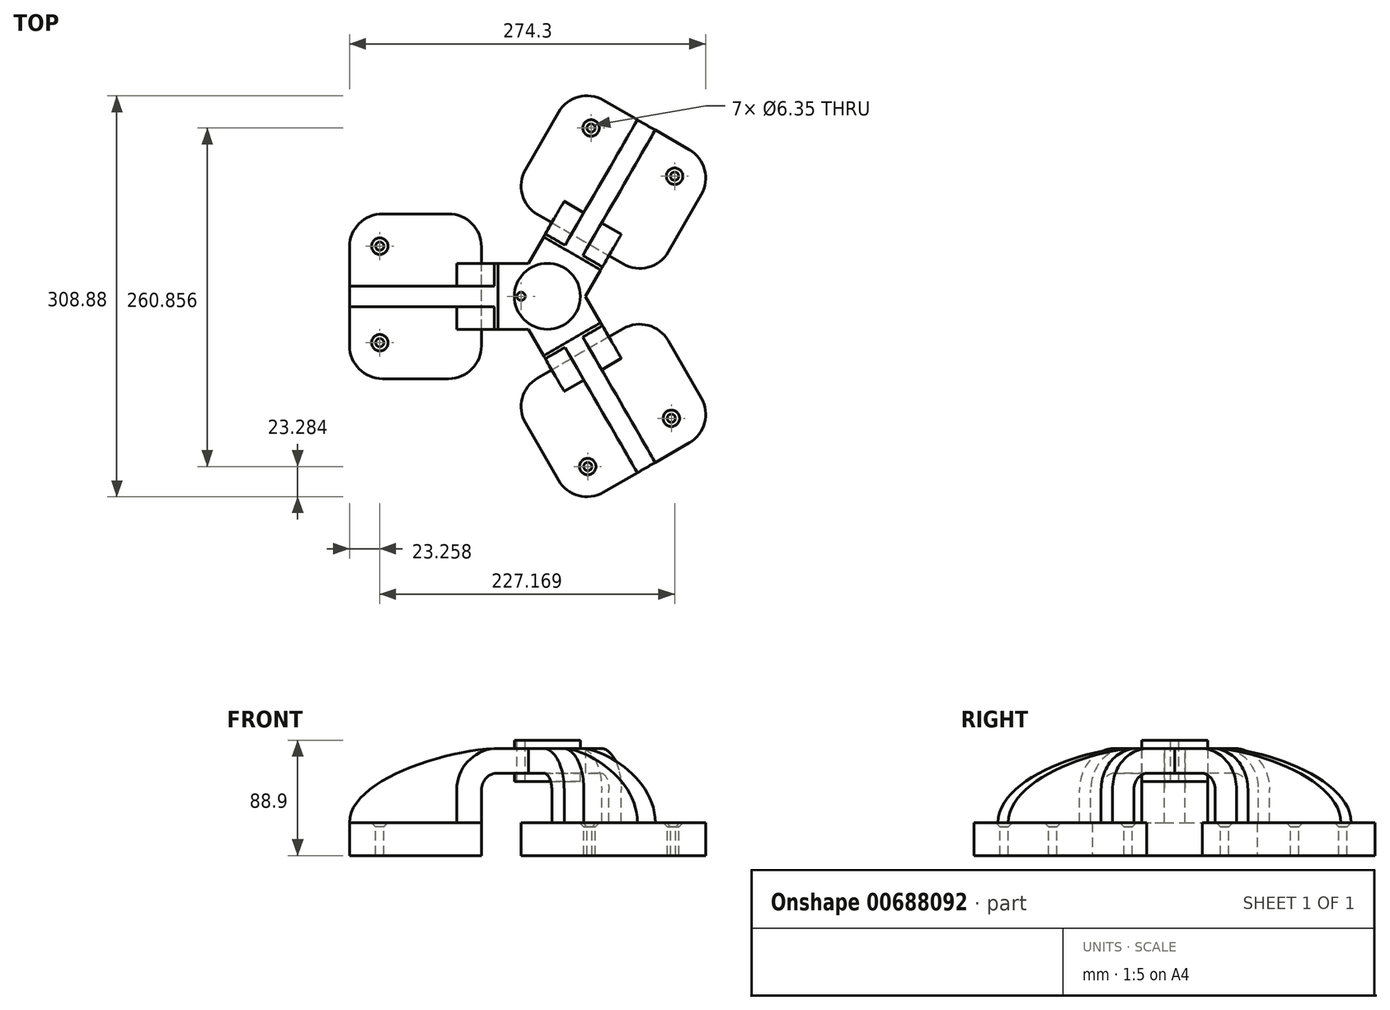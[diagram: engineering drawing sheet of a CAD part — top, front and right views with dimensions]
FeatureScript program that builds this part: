
annotation { "Feature Type Name" : "Feature", "Feature Type Description" : "" }
export const myFeature = defineFeature(function(context is Context, id is Id, definition is map)
    precondition{}
    {
        {
            var Q0;
            Q0=qCreatedBy(makeId("Front.planeOp"),FACE);
            var sketch = newSketch(context, id + "F0", { "sketchPlane" : qUnion([Q0])});
            skLineSegment(sketch, "E0.bottom", {"start": v(50.8, 12.7) * mm, "end": v(-50.8, 12.7) * mm});
            skLineSegment(sketch, "E0.top", {"start": v(50.8, -12.7) * mm, "end": v(-50.8, -12.7) * mm});
            skLineSegment(sketch, "E0.left", {"start": v(50.8, 12.7) * mm, "end": v(50.8, -12.7) * mm});
            skLineSegment(sketch, "E0.right", {"start": v(-50.8, 12.7) * mm, "end": v(-50.8, -12.7) * mm});
            skPoint(sketch, "E0.middle", {"position": v(0, 0) * mm});
            skLineSegment(sketch, "E1.bottom", {"start": v(76.2, 76.2) * mm, "end": v(127, 76.2) * mm});
            skLineSegment(sketch, "E1.top", {"start": v(76.2, 44.45) * mm, "end": v(127, 44.45) * mm});
            skLineSegment(sketch, "E1.left", {"start": v(76.2, 76.2) * mm, "end": v(76.2, 44.45) * mm});
            skLineSegment(sketch, "E1.right", {"start": v(127, 76.2) * mm, "end": v(127, 44.45) * mm});
            skLineSegment(sketch, "E2", {"start": v(50.8, 12.7) * mm, "end": v(50.8, 38.1) * mm});
            skArc(sketch, "E3", {"start": v(50.8, 38.1) * mm, "mid": v(54.52, 47.08) * mm, "end": v(63.5, 50.8) * mm});
            skLineSegment(sketch, "E4", {"start": v(63.5, 50.8) * mm, "end": v(101.6, 50.8) * mm});
            skLineSegment(sketch, "E5.0", {"start": v(63.5, 69.85) * mm, "end": v(101.6, 69.85) * mm});
            skArc(sketch, "E5.1", {"start": v(31.75, 38.1) * mm, "mid": v(41.05, 60.55) * mm, "end": v(63.5, 69.85) * mm});
            skLineSegment(sketch, "E5.2", {"start": v(31.75, 12.7) * mm, "end": v(31.75, 38.1) * mm});
            skFitSpline(sketch, "E6", {"points": [v(-50.8, 12.7) * mm, v(63.5, 69.85) * mm], "startDerivative": vector(-1.6, 93) * mm, "endDerivative": vector(136.62, 4.63) * mm});
            skLineSegment(sketch, "E7", {"start": v(101.6, 76.2) * mm, "end": v(101.6, 44.45) * mm});
            skSolve(sketch);
        }
        {
            var Q0;
            Q0=makeQuery(id+"F0.imprint","IMPRINT",FACE,{"disambiguationData":[TD([[makeQuery(id+"F0.imprint","IMPRINT",EDGE,{"derivedFrom":sQuery(id+"F0.wireOp",EDGE,"E0.top")}),-1.0]])]});
            extrude(context, id + "F1", {"entities" : qUnion([Q0]), "endBound" : BoundingType.SYMMETRIC, "depth" : 127 * mm, "offsetDistance" : 25.4 * mm});
        }
        {
            var Q0;
            {var subQ1=sQuery(id+"F0.wireOp",EDGE,"E2");Q0=makeQuery(id+"F0.imprint","IMPRINT",FACE,{"disambiguationData":[TD([[makeQuery(id+"F0.imprint","IMPRINT",EDGE,{"derivedFrom":subQ1}),1.0]])]});}
            var Q1;
            {var subQ0=sQuery(id+"F0.wireOp",EDGE,"E5.0");var subQ1=sQuery(id+"F0.wireOp",EDGE,"E1.left");var subQ2=makeQuery(id+"F0.imprint","INTERSECT",VERTEX,{"derivedFrom":[subQ1,subQ0]});Q1=makeQuery(id+"F0.imprint","IMPRINT",FACE,{"disambiguationData":[TD([[makeQuery(id+"F0.imprint","IMPRINT",EDGE,{"disambiguationData":[TD([[subQ2,-1.0]])],"derivedFrom":subQ1}),1.0]])]});}
            extrude(context, id + "F2", {"entities" : qUnion([Q0, Q1]), "operationType" : NewBodyOperationType.ADD, "endBound" : BoundingType.SYMMETRIC, "depth" : 50.8 * mm, "offsetDistance" : 25.4 * mm});
        }
        {
            var Q0;
            {var subQ3=sQuery(id+"F0.wireOp",EDGE,"E5.2");Q0=makeQuery(id+"F0.imprint","IMPRINT",FACE,{"disambiguationData":[TD([[makeQuery(id+"F0.imprint","IMPRINT",EDGE,{"derivedFrom":subQ3}),1.0]])]});}
            extrude(context, id + "F3", {"entities" : qUnion([Q0]), "operationType" : NewBodyOperationType.ADD, "endBound" : BoundingType.SYMMETRIC, "depth" : 15.88 * mm, "offsetDistance" : 25.4 * mm});
        }
        {
            var Q0;
            {var subQ4=sQuery(id+"F0.wireOp",EDGE,"E1.right");Q0=makeQuery(id+"F0.imprint","IMPRINT",FACE,{"disambiguationData":[TD([[makeQuery(id+"F0.imprint","IMPRINT",EDGE,{"derivedFrom":subQ4}),-1.0]])]});}
            var Q1;
            Q1=sQuery(id+"F0.wireOp",EDGE,"E7");
            revolve(context, id + "F4", {"operationType" : NewBodyOperationType.ADD, "entities" : qUnion([Q0]), "axis" : qUnion([Q1]), "revolveType" : RevolveType.FULL});
        }
        {
            var Q0;
            {var subQ4=sQuery(id+"F0.wireOp",EDGE,"E0.bottom");var subQ5=sQuery(id+"F0.wireOp",EDGE,"E0.right");var subQ6=sQuery(id+"F0.wireOp",EDGE,"E0.left");Q0=makeQuery(id+"F3.boolean.opBoolean","SPLIT",FACE,{"disambiguationData":[TD([makeQuery(id+"F1.opExtrude","CAP_FACE",FACE,{"disambiguationData":[OSD([subQ4,sQuery(id+"F0.wireOp",EDGE,"E0.top"),subQ6,subQ5])],"isStart":false})])],"derivedFrom":makeQuery(id+"F1.opExtrude","SWEPT_FACE",FACE,{"disambiguationData":[OSD([subQ4])]})});}
            var sketch = newSketch(context, id + "F5", { "sketchPlane" : qUnion([Q0])});
            skPoint(sketch, "E8", {"position": v(-27.54, -35.72) * mm});
            skPoint(sketch, "E8.positionSnap0", {"position": v(-50.8, -35.72) * mm});
            skPoint(sketch, "E9", {"position": v(-27.54, 38.63) * mm});
            skSolve(sketch);
        }
        {
            var Q0;
            Q0=sQuery(id+"F5.wireOp",VERTEX,"E8");
            var Q1;
            Q1=sQuery(id+"F5.wireOp",VERTEX,"E9");
            var Q2;
            Q2=makeQuery(id+"F1.opExtrude","SWEPT_BODY",BODY,{"disambiguationData":[OSD([sQuery(id+"F0.wireOp",EDGE,"E0.bottom"),sQuery(id+"F0.wireOp",EDGE,"E0.top"),sQuery(id+"F0.wireOp",EDGE,"E0.left"),sQuery(id+"F0.wireOp",EDGE,"E0.right")])]});
            hole(context, id + "F6", {"style" : HoleStyle.C_SINK, "endStyle" : HoleEndStyle.THROUGH, "holeDiameter" : 6.35 * mm, "cSinkDiameter" : 12.7 * mm, "cSinkAngle" : 90 * degree, "majorDiameter" : 6.35 * mm, "isTappedThrough" : true, "tappedDepth" : 12.7 * mm, "tapClearance" : 3, "locations" : qUnion([Q0, Q1]), "scope" : qUnion([Q2])});
        }
        {
            var Q0;
            Q0=makeQuery(id+"F1.opExtrude","SWEPT_BODY",BODY,{"disambiguationData":[OSD([sQuery(id+"F0.wireOp",EDGE,"E0.bottom"),sQuery(id+"F0.wireOp",EDGE,"E0.top"),sQuery(id+"F0.wireOp",EDGE,"E0.left"),sQuery(id+"F0.wireOp",EDGE,"E0.right")])]});
            var Q1;
            Q1=sQuery(id+"F0.wireOp",EDGE,"E7");
            circularPattern(context, id + "F7", {"operationType" : NewBodyOperationType.ADD, "entities" : qUnion([Q0]), "axis" : qUnion([Q1]), "angle" : 360 * degree, "instanceCount" : 3, "equalSpace" : true});
        }
        {
            var Q0;
            Q0=makeQuery(id+"F4.opRevolve","SWEPT_FACE",FACE,{"disambiguationData":[OSD([sQuery(id+"F0.wireOp",EDGE,"E1.bottom")])]});
            var sketch = newSketch(context, id + "F8", { "sketchPlane" : qUnion([Q0])});
            skPoint(sketch, "E10", {"position": v(81.33, 0) * mm});
            skSolve(sketch);
        }
        {
            var Q0;
            Q0=sQuery(id+"F8.wireOp",VERTEX,"E10");
            var Q1;
            Q1=makeQuery(id+"F1.opExtrude","SWEPT_BODY",BODY,{"disambiguationData":[OSD([sQuery(id+"F0.wireOp",EDGE,"E0.bottom"),sQuery(id+"F0.wireOp",EDGE,"E0.top"),sQuery(id+"F0.wireOp",EDGE,"E0.left"),sQuery(id+"F0.wireOp",EDGE,"E0.right")])]});
            hole(context, id + "F9", {"style" : HoleStyle.SIMPLE, "endStyle" : HoleEndStyle.THROUGH, "holeDiameter" : 6.35 * mm, "majorDiameter" : 6.35 * mm, "isTappedThrough" : true, "tappedDepth" : 12.7 * mm, "tapClearance" : 3, "locations" : qUnion([Q0]), "scope" : qUnion([Q1])});
        }
        {
            var Q0;
            Q0=makeQuery(id+"F1.opExtrude","CAP_EDGE",EDGE,{"disambiguationData":[OSD([sQuery(id+"F0.wireOp",EDGE,"E0.right")])],"isStart":false});
            var Q1;
            Q1=makeQuery(id+"F7.opPattern","COPY",EDGE,{"derivedFrom":makeQuery(id+"F1.opExtrude","CAP_EDGE",EDGE,{"disambiguationData":[OSD([sQuery(id+"F0.wireOp",EDGE,"E0.right")])],"isStart":true}),"instanceName":"2"});
            var Q2;
            Q2=makeQuery(id+"F7.opPattern","COPY",EDGE,{"derivedFrom":makeQuery(id+"F1.opExtrude","CAP_EDGE",EDGE,{"disambiguationData":[OSD([sQuery(id+"F0.wireOp",EDGE,"E0.right")])],"isStart":false}),"instanceName":"2"});
            var Q3;
            Q3=makeQuery(id+"F7.opPattern","COPY",EDGE,{"derivedFrom":makeQuery(id+"F1.opExtrude","CAP_EDGE",EDGE,{"disambiguationData":[OSD([sQuery(id+"F0.wireOp",EDGE,"E0.right")])],"isStart":true}),"instanceName":"1"});
            var Q4;
            Q4=makeQuery(id+"F7.opPattern","COPY",EDGE,{"derivedFrom":makeQuery(id+"F1.opExtrude","CAP_EDGE",EDGE,{"disambiguationData":[OSD([sQuery(id+"F0.wireOp",EDGE,"E0.left")])],"isStart":true}),"instanceName":"1"});
            var Q5;
            Q5=makeQuery(id+"F7.opPattern","COPY",EDGE,{"derivedFrom":makeQuery(id+"F1.opExtrude","CAP_EDGE",EDGE,{"disambiguationData":[OSD([sQuery(id+"F0.wireOp",EDGE,"E0.left")])],"isStart":false}),"instanceName":"2"});
            var Q6;
            Q6=makeQuery(id+"F1.opExtrude","CAP_EDGE",EDGE,{"disambiguationData":[OSD([sQuery(id+"F0.wireOp",EDGE,"E0.left")])],"isStart":false});
            var Q7;
            Q7=makeQuery(id+"F7.opPattern","COPY",EDGE,{"derivedFrom":makeQuery(id+"F1.opExtrude","CAP_EDGE",EDGE,{"disambiguationData":[OSD([sQuery(id+"F0.wireOp",EDGE,"E0.right")])],"isStart":false}),"instanceName":"1"});
            var Q8;
            Q8=makeQuery(id+"F7.opPattern","COPY",EDGE,{"derivedFrom":makeQuery(id+"F1.opExtrude","CAP_EDGE",EDGE,{"disambiguationData":[OSD([sQuery(id+"F0.wireOp",EDGE,"E0.left")])],"isStart":false}),"instanceName":"1"});
            var Q9;
            Q9=makeQuery(id+"F7.opPattern","COPY",EDGE,{"derivedFrom":makeQuery(id+"F1.opExtrude","CAP_EDGE",EDGE,{"disambiguationData":[OSD([sQuery(id+"F0.wireOp",EDGE,"E0.left")])],"isStart":true}),"instanceName":"2"});
            var Q10;
            Q10=makeQuery(id+"F1.opExtrude","CAP_EDGE",EDGE,{"disambiguationData":[OSD([sQuery(id+"F0.wireOp",EDGE,"E0.left")])],"isStart":true});
            var Q11;
            Q11=makeQuery(id+"F1.opExtrude","CAP_EDGE",EDGE,{"disambiguationData":[OSD([sQuery(id+"F0.wireOp",EDGE,"E0.right")])],"isStart":true});
            fillet(context, id + "F10", {"entities" : qUnion([Q0, Q1, Q2, Q3, Q4, Q5, Q6, Q7, Q8, Q9, Q10, Q11]), "radius" : 25.4 * mm, "tangentPropagation" : true, "allowEdgeOverflow" : false});
        }
    });
